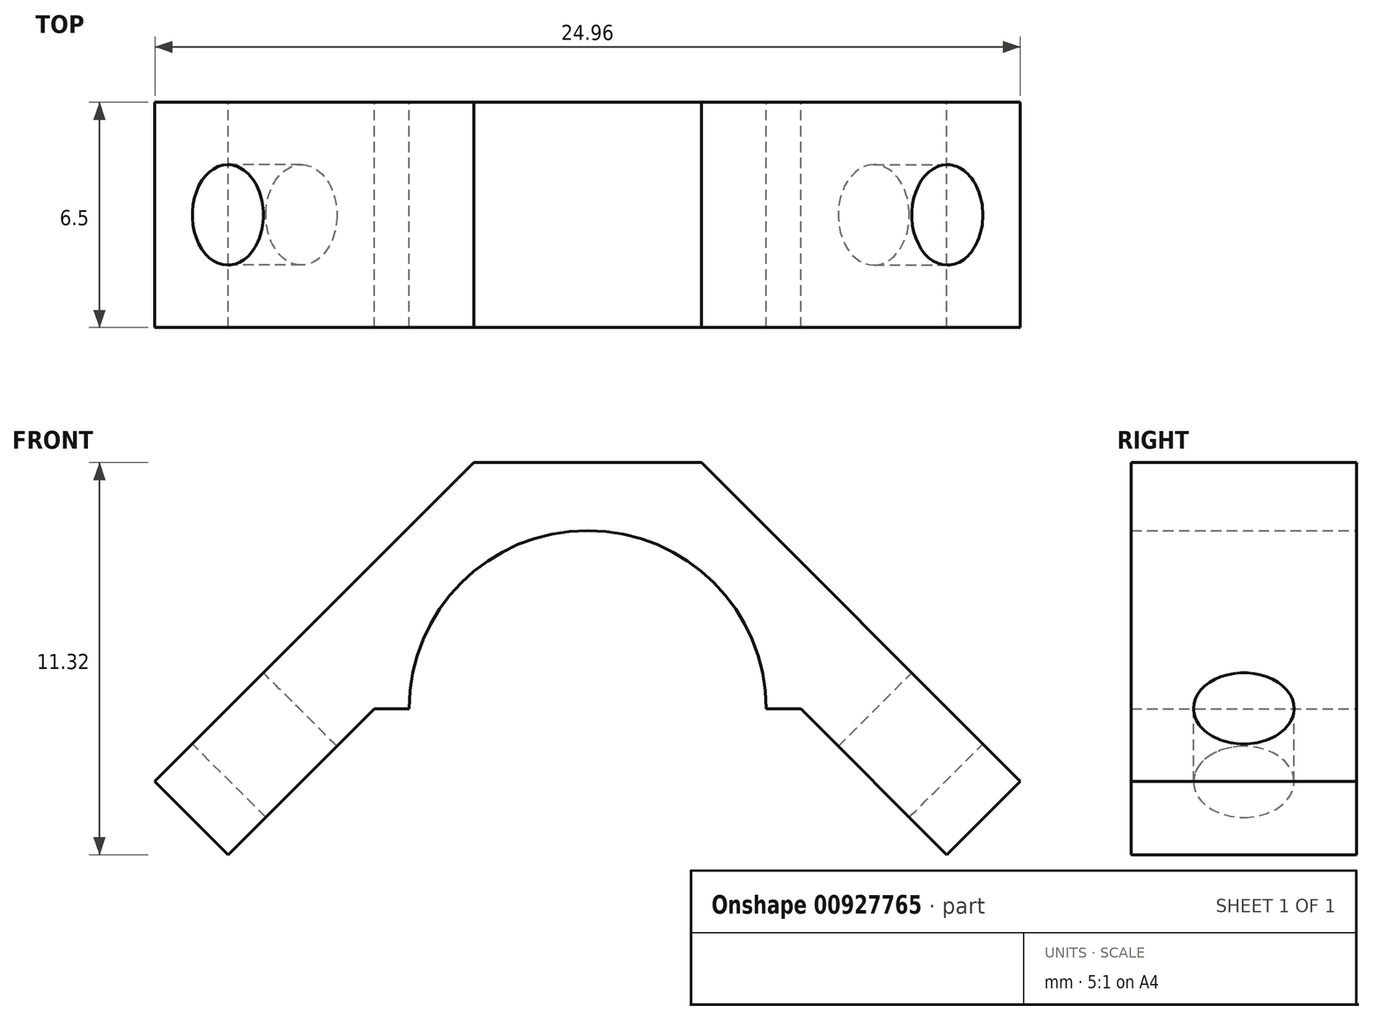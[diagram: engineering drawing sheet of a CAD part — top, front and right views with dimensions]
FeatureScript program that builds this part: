
annotation { "Feature Type Name" : "Feature", "Feature Type Description" : "" }
export const myFeature = defineFeature(function(context is Context, id is Id, definition is map)
    precondition{}
    {
        {
            var Q0;
            Q0=qCreatedBy(makeId("Front.planeOp"),FACE);
            var sketch = newSketch(context, id + "F0", { "sketchPlane" : qUnion([Q0])});
            skArc(sketch, "E0", {"start": v(5.15, 0) * mm, "mid": v(0, 5.15) * mm, "end": v(-5.15, 0) * mm});
            skLineSegment(sketch, "E1", {"start": v(-5.15, 0) * mm, "end": v(-6.15, 0) * mm});
            skLineSegment(sketch, "E2", {"start": v(-6.15, 0) * mm, "end": v(-5.15, 0) * mm});
            skLineSegment(sketch, "E3", {"start": v(6.15, 0) * mm, "end": v(10.36, -4.21) * mm});
            skLineSegment(sketch, "E4", {"start": v(-6.15, 0) * mm, "end": v(-10.36, -4.21) * mm});
            skLineSegment(sketch, "E5.trimOffspring", {"start": v(5.15, 0) * mm, "end": v(6.15, 0) * mm});
            skLineSegment(sketch, "E6", {"start": v(-10.36, -4.21) * mm, "end": v(-12.48, -2.1) * mm});
            skLineSegment(sketch, "E7", {"start": v(-12.48, -2.1) * mm, "end": v(-3.28, 7.11) * mm});
            skLineSegment(sketch, "E8", {"start": v(10.36, -4.21) * mm, "end": v(12.48, -2.1) * mm});
            skLineSegment(sketch, "E9", {"start": v(12.48, -2.1) * mm, "end": v(3.28, 7.11) * mm});
            skLineSegment(sketch, "E10", {"start": v(-3.28, 7.11) * mm, "end": v(3.28, 7.11) * mm});
            skSolve(sketch);
        }
        {
            var Q0;
            Q0=makeQuery(id+"F0.imprint","IMPRINT",FACE,{"disambiguationData":[TD([[makeQuery(id+"F0.imprint","IMPRINT",EDGE,{"derivedFrom":sQuery(id+"F0.wireOp",EDGE,"E0")}),-1.0]])]});
            extrude(context, id + "F1", {"entities" : qUnion([Q0]), "depth" : 6.5 * mm, "offsetDistance" : 25 * mm});
        }
        {
            var Q0;
            Q0=makeQuery(id+"F1.opExtrude","SWEPT_FACE",FACE,{"disambiguationData":[OSD([sQuery(id+"F0.wireOp",EDGE,"E7")])]});
            var sketch = newSketch(context, id + "F2", { "sketchPlane" : qUnion([Q0])});
            skLineSegment(sketch, "E11", {"start": v(0, -10.3) * mm, "end": v(0, -4.35) * mm});
            skLineSegment(sketch, "E12", {"start": v(0, -4.35) * mm, "end": v(6.5, -4.35) * mm});
            skLineSegment(sketch, "E13", {"start": v(3.25, -4.35) * mm, "end": v(3.25, -10.3) * mm, "construction": true});
            skLineSegment(sketch, "E14", {"start": v(0, -7.33) * mm, "end": v(6.5, -7.33) * mm, "construction": true});
            skPoint(sketch, "E14.endSnap0", {"position": v(3.25, -7.33) * mm});
            skCircle(sketch, "E15", {"center": v(3.25, -7.33) * mm, "radius": 1.45 * mm});
            skSolve(sketch);
        }
        {
            var Q0;
            Q0=makeQuery(id+"F2.imprint","IMPRINT",FACE,{"disambiguationData":[TD([[makeQuery(id+"F2.imprint","IMPRINT",EDGE,{"derivedFrom":sQuery(id+"F2.wireOp",EDGE,"E15")}),1.0]])]});
            extrude(context, id + "F3", {"entities" : qUnion([Q0]), "operationType" : NewBodyOperationType.REMOVE, "oppositeDirection" : true, "depth" : 25 * mm, "offsetDistance" : 25 * mm});
        }
        {
            var Q0;
            Q0=makeQuery(id+"F1.opExtrude","SWEPT_FACE",FACE,{"disambiguationData":[OSD([sQuery(id+"F0.wireOp",EDGE,"E9")])]});
            var sketch = newSketch(context, id + "F4", { "sketchPlane" : qUnion([Q0])});
            skLineSegment(sketch, "E16", {"start": v(-6.5, -10.3) * mm, "end": v(-6.5, -4.35) * mm});
            skLineSegment(sketch, "E17", {"start": v(-6.5, -4.35) * mm, "end": v(-1, -4.35) * mm});
            skPoint(sketch, "E18.endSnap0", {"position": v(-3.25, -7.33) * mm});
            skCircle(sketch, "E19", {"center": v(-3.25, -7.33) * mm, "radius": 1.45 * mm});
            skLineSegment(sketch, "E20", {"start": v(-6.5, -7.33) * mm, "end": v(0, -7.33) * mm, "construction": true});
            skSolve(sketch);
        }
        {
            var Q0;
            Q0=makeQuery(id+"F4.imprint","IMPRINT",FACE,{"disambiguationData":[TD([[makeQuery(id+"F4.imprint","IMPRINT",EDGE,{"derivedFrom":sQuery(id+"F4.wireOp",EDGE,"E19")}),1.0]])]});
            extrude(context, id + "F5", {"entities" : qUnion([Q0]), "operationType" : NewBodyOperationType.REMOVE, "oppositeDirection" : true, "depth" : 25 * mm, "offsetDistance" : 25 * mm});
        }
    });
